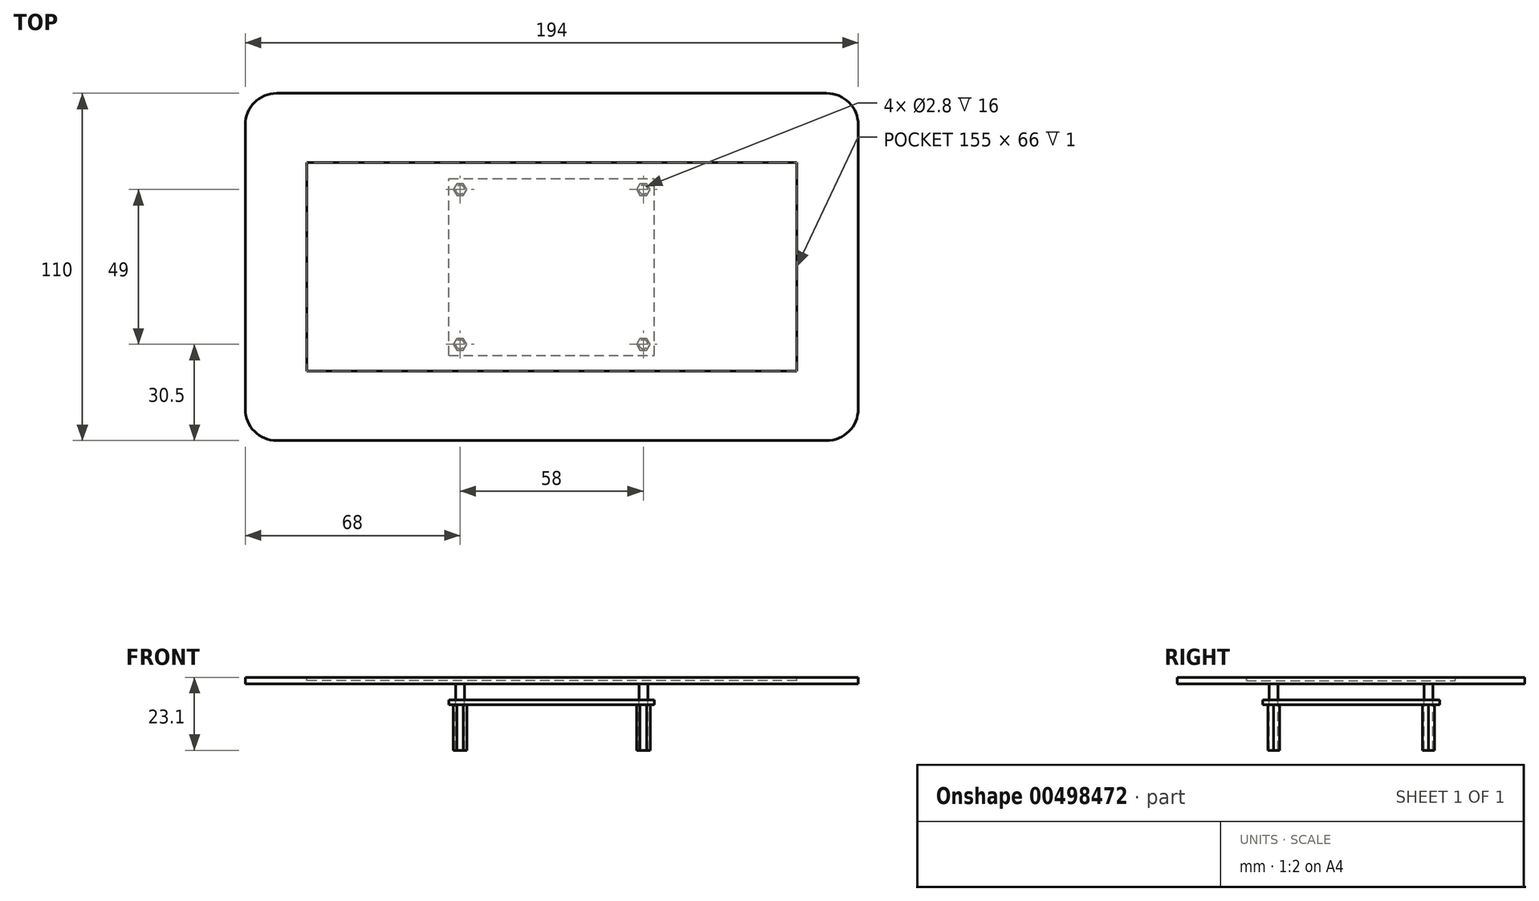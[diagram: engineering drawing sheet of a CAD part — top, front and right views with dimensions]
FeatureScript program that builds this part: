
annotation { "Feature Type Name" : "Feature", "Feature Type Description" : "" }
export const myFeature = defineFeature(function(context is Context, id is Id, definition is map)
    precondition{}
    {
        {
            var Q0;
            Q0=qCreatedBy(makeId("Top.planeOp"),FACE);
            var sketch = newSketch(context, id + "F0", { "sketchPlane" : qUnion([Q0])});
            skLineSegment(sketch, "E0.bottom", {"start": v(-87, 55) * mm, "end": v(87, 55) * mm});
            skLineSegment(sketch, "E0.top", {"start": v(-87, -55) * mm, "end": v(87, -55) * mm});
            skLineSegment(sketch, "E0.left", {"start": v(-97, 45) * mm, "end": v(-97, -45) * mm});
            skLineSegment(sketch, "E0.right", {"start": v(97, 45) * mm, "end": v(97, -45) * mm});
            skPoint(sketch, "E0.middle", {"position": v(0, 0) * mm});
            skPoint(sketch, "E1.visualSharp", {"position": v(-97, 55) * mm});
            skArc(sketch, "E1.filletArc", {"start": v(-87, 55) * mm, "mid": v(-94.07, 52.07) * mm, "end": v(-97, 45) * mm});
            skPoint(sketch, "E2.visualSharp", {"position": v(-97, -55) * mm});
            skArc(sketch, "E2.filletArc", {"start": v(-97, -45) * mm, "mid": v(-94.07, -52.07) * mm, "end": v(-87, -55) * mm});
            skPoint(sketch, "E3.visualSharp", {"position": v(97, -55) * mm});
            skArc(sketch, "E3.filletArc", {"start": v(87, -55) * mm, "mid": v(94.07, -52.07) * mm, "end": v(97, -45) * mm});
            skPoint(sketch, "E4.visualSharp", {"position": v(97, 55) * mm});
            skArc(sketch, "E4.filletArc", {"start": v(97, 45) * mm, "mid": v(94.07, 52.07) * mm, "end": v(87, 55) * mm});
            skSolve(sketch);
        }
        {
            var Q0;
            Q0 = qSketchRegion(id + "F0", true);
            extrude(context, id + "F1", {"entities" : qUnion([Q0]), "depth" : 2 * mm});
        }
        {
            var Q0;
            Q0=makeQuery(id+"F1.opExtrude","CAP_FACE",FACE,{"disambiguationData":[OSD([sQuery(id+"F0.wireOp",EDGE,"E0.bottom"),sQuery(id+"F0.wireOp",EDGE,"E0.top"),sQuery(id+"F0.wireOp",EDGE,"E0.left"),sQuery(id+"F0.wireOp",EDGE,"E0.right"),sQuery(id+"F0.wireOp",EDGE,"E1.filletArc"),sQuery(id+"F0.wireOp",EDGE,"E2.filletArc"),sQuery(id+"F0.wireOp",EDGE,"E3.filletArc"),sQuery(id+"F0.wireOp",EDGE,"E4.filletArc")])],"isStart":false});
            var sketch = newSketch(context, id + "F2", { "sketchPlane" : qUnion([Q0])});
            skLineSegment(sketch, "E5.bottom", {"start": v(77.5, -33) * mm, "end": v(-77.5, -33) * mm});
            skLineSegment(sketch, "E5.top", {"start": v(77.5, 33) * mm, "end": v(-77.5, 33) * mm});
            skLineSegment(sketch, "E5.left", {"start": v(77.5, -33) * mm, "end": v(77.5, 33) * mm});
            skLineSegment(sketch, "E5.right", {"start": v(-77.5, -33) * mm, "end": v(-77.5, 33) * mm});
            skPoint(sketch, "E5.middle", {"position": v(0, 0) * mm});
            skSolve(sketch);
        }
        {
            var Q0;
            Q0=makeQuery(id+"F2.imprint","IMPRINT",FACE,{"disambiguationData":[TD([[makeQuery(id+"F2.imprint","IMPRINT",EDGE,{"derivedFrom":sQuery(id+"F2.wireOp",EDGE,"E5.bottom")}),-1.0]])]});
            extrude(context, id + "F3", {"entities" : qUnion([Q0]), "operationType" : NewBodyOperationType.REMOVE, "oppositeDirection" : true, "depth" : 1 * mm});
        }
        {
            var Q0;
            Q0=makeQuery(id+"F1.opExtrude","CAP_FACE",FACE,{"disambiguationData":[OSD([sQuery(id+"F0.wireOp",EDGE,"E0.bottom"),sQuery(id+"F0.wireOp",EDGE,"E0.top"),sQuery(id+"F0.wireOp",EDGE,"E0.left"),sQuery(id+"F0.wireOp",EDGE,"E0.right"),sQuery(id+"F0.wireOp",EDGE,"E1.filletArc"),sQuery(id+"F0.wireOp",EDGE,"E2.filletArc"),sQuery(id+"F0.wireOp",EDGE,"E3.filletArc"),sQuery(id+"F0.wireOp",EDGE,"E4.filletArc")])],"isStart":true});
            var sketch = newSketch(context, id + "F4", { "sketchPlane" : qUnion([Q0])});
            skLineSegment(sketch, "E6.bottom", {"start": v(-29, 24.5) * mm, "end": v(29, 24.5) * mm, "construction": true});
            skLineSegment(sketch, "E6.top", {"start": v(-29, -24.5) * mm, "end": v(29, -24.5) * mm, "construction": true});
            skLineSegment(sketch, "E6.left", {"start": v(-29, 24.5) * mm, "end": v(-29, -24.5) * mm, "construction": true});
            skLineSegment(sketch, "E6.right", {"start": v(29, 24.5) * mm, "end": v(29, -24.5) * mm, "construction": true});
            skPoint(sketch, "E6.middle", {"position": v(0, 0) * mm});
            skCircle(sketch, "E7", {"center": v(-29, 24.5) * mm, "radius": 1.4 * mm});
            skCircle(sketch, "E8", {"center": v(29, 24.5) * mm, "radius": 1.4 * mm});
            skCircle(sketch, "E9", {"center": v(-29, -24.5) * mm, "radius": 1.4 * mm});
            skCircle(sketch, "E10", {"center": v(29, -24.5) * mm, "radius": 1.4 * mm});
            skSolve(sketch);
        }
        {
            var Q0;
            Q0=makeQuery(id+"F4.imprint","IMPRINT",FACE,{"disambiguationData":[TD([[makeQuery(id+"F4.imprint","IMPRINT",EDGE,{"derivedFrom":sQuery(id+"F4.wireOp",EDGE,"E7")}),1.0]])]});
            var Q1;
            Q1=makeQuery(id+"F4.imprint","IMPRINT",FACE,{"disambiguationData":[TD([[makeQuery(id+"F4.imprint","IMPRINT",EDGE,{"derivedFrom":sQuery(id+"F4.wireOp",EDGE,"E9")}),1.0]])]});
            var Q2;
            Q2=makeQuery(id+"F4.imprint","IMPRINT",FACE,{"disambiguationData":[TD([[makeQuery(id+"F4.imprint","IMPRINT",EDGE,{"derivedFrom":sQuery(id+"F4.wireOp",EDGE,"E10")}),1.0]])]});
            var Q3;
            Q3=makeQuery(id+"F4.imprint","IMPRINT",FACE,{"disambiguationData":[TD([[makeQuery(id+"F4.imprint","IMPRINT",EDGE,{"derivedFrom":sQuery(id+"F4.wireOp",EDGE,"E8")}),1.0]])]});
            extrude(context, id + "F5", {"entities" : qUnion([Q0, Q1, Q2, Q3]), "operationType" : NewBodyOperationType.ADD, "depth" : 5.1 * mm});
        }
        {
            var Q0;
            Q0=makeQuery(id+"F5.opExtrude","CAP_FACE",FACE,{"disambiguationData":[OSD([sQuery(id+"F4.wireOp",EDGE,"E7")])],"isStart":false});
            var sketch = newSketch(context, id + "F6", { "sketchPlane" : qUnion([Q0])});
            skLineSegment(sketch, "E11.bottom", {"start": v(-29, 24.5) * mm, "end": v(29, 24.5) * mm, "construction": true});
            skLineSegment(sketch, "E11.top", {"start": v(-29, -24.5) * mm, "end": v(29, -24.5) * mm, "construction": true});
            skLineSegment(sketch, "E11.left", {"start": v(-29, 24.5) * mm, "end": v(-29, -24.5) * mm, "construction": true});
            skLineSegment(sketch, "E11.right", {"start": v(29, 24.5) * mm, "end": v(29, -24.5) * mm, "construction": true});
            skPoint(sketch, "E11.middle", {"position": v(0, 0) * mm});
            skLineSegment(sketch, "E12.bottom", {"start": v(-32.5, 28) * mm, "end": v(32.5, 28) * mm});
            skLineSegment(sketch, "E12.top", {"start": v(-32.5, -28) * mm, "end": v(32.5, -28) * mm});
            skLineSegment(sketch, "E12.left", {"start": v(-32.5, 28) * mm, "end": v(-32.5, -28) * mm});
            skLineSegment(sketch, "E12.right", {"start": v(32.5, 28) * mm, "end": v(32.5, -28) * mm});
            skCircle(sketch, "E13", {"center": v(-29, 24.5) * mm, "radius": 1.4 * mm});
            skCircle(sketch, "E14", {"center": v(29, 24.5) * mm, "radius": 1.4 * mm});
            skCircle(sketch, "E15", {"center": v(-29, -24.5) * mm, "radius": 1.4 * mm});
            skCircle(sketch, "E16", {"center": v(29, -24.5) * mm, "radius": 1.4 * mm});
            skSolve(sketch);
        }
        {
            var Q0;
            Q0 = qSketchRegion(id + "F6", true);
            extrude(context, id + "F7", {"entities" : qUnion([Q0]), "depth" : 1.6 * mm});
        }
        {
            var Q0;
            Q0=makeQuery(id+"F7.opExtrude","CAP_FACE",FACE,{"disambiguationData":[OSD([sQuery(id+"F6.wireOp",EDGE,"E12.bottom"),sQuery(id+"F6.wireOp",EDGE,"E12.top"),sQuery(id+"F6.wireOp",EDGE,"E12.left"),sQuery(id+"F6.wireOp",EDGE,"E12.right"),sQuery(id+"F6.wireOp",EDGE,"E13"),sQuery(id+"F6.wireOp",EDGE,"E14"),sQuery(id+"F6.wireOp",EDGE,"E15"),sQuery(id+"F6.wireOp",EDGE,"E16")])],"isStart":false});
            var sketch = newSketch(context, id + "F8", { "sketchPlane" : qUnion([Q0])});
            skCircle(sketch, "E17", {"center": v(-29, 24.5) * mm, "radius": 1.4 * mm});
            skCircle(sketch, "E18", {"center": v(29, 24.5) * mm, "radius": 1.4 * mm});
            skCircle(sketch, "E19", {"center": v(-29, -24.5) * mm, "radius": 1.4 * mm});
            skCircle(sketch, "E20", {"center": v(29, -24.5) * mm, "radius": 1.4 * mm});
            skCircle(sketch, "E21.cCircle", {"center": v(-29, 24.5) * mm, "radius": 2.15 * mm, "construction": true});
            skLineSegment(sketch, "E21.0", {"start": v(-26.85, 24.5) * mm, "end": v(-27.92, 22.64) * mm});
            skLineSegment(sketch, "E21.1", {"start": v(-27.92, 22.64) * mm, "end": v(-30.07, 22.64) * mm});
            skLineSegment(sketch, "E21.2", {"start": v(-30.07, 22.64) * mm, "end": v(-31.15, 24.5) * mm});
            skLineSegment(sketch, "E21.3", {"start": v(-31.15, 24.5) * mm, "end": v(-30.07, 26.36) * mm});
            skLineSegment(sketch, "E21.4", {"start": v(-30.07, 26.36) * mm, "end": v(-27.92, 26.36) * mm});
            skLineSegment(sketch, "E21.5", {"start": v(-27.92, 26.36) * mm, "end": v(-26.85, 24.5) * mm});
            skCircle(sketch, "E22.cCircle", {"center": v(29, 24.5) * mm, "radius": 2.15 * mm, "construction": true});
            skLineSegment(sketch, "E22.0", {"start": v(26.85, 24.5) * mm, "end": v(27.93, 26.36) * mm});
            skLineSegment(sketch, "E22.1", {"start": v(27.93, 26.36) * mm, "end": v(30.07, 26.36) * mm});
            skLineSegment(sketch, "E22.2", {"start": v(30.07, 26.36) * mm, "end": v(31.15, 24.5) * mm});
            skLineSegment(sketch, "E22.3", {"start": v(31.15, 24.5) * mm, "end": v(30.08, 22.64) * mm});
            skLineSegment(sketch, "E22.4", {"start": v(30.07, 22.64) * mm, "end": v(27.92, 22.64) * mm});
            skLineSegment(sketch, "E22.5", {"start": v(27.93, 22.64) * mm, "end": v(26.85, 24.5) * mm});
            skCircle(sketch, "E23.cCircle", {"center": v(29, -24.5) * mm, "radius": 2.15 * mm, "construction": true});
            skLineSegment(sketch, "E23.0", {"start": v(26.85, -24.5) * mm, "end": v(27.92, -22.64) * mm});
            skLineSegment(sketch, "E23.1", {"start": v(27.93, -22.64) * mm, "end": v(30.08, -22.64) * mm});
            skLineSegment(sketch, "E23.2", {"start": v(30.07, -22.64) * mm, "end": v(31.15, -24.5) * mm});
            skLineSegment(sketch, "E23.3", {"start": v(31.15, -24.5) * mm, "end": v(30.07, -26.36) * mm});
            skLineSegment(sketch, "E23.4", {"start": v(30.08, -26.36) * mm, "end": v(27.92, -26.36) * mm});
            skLineSegment(sketch, "E23.5", {"start": v(27.93, -26.36) * mm, "end": v(26.85, -24.5) * mm});
            skCircle(sketch, "E24.cCircle", {"center": v(-29, -24.5) * mm, "radius": 2.15 * mm, "construction": true});
            skLineSegment(sketch, "E24.0", {"start": v(-26.85, -24.5) * mm, "end": v(-27.93, -26.36) * mm});
            skLineSegment(sketch, "E24.1", {"start": v(-27.93, -26.36) * mm, "end": v(-30.07, -26.36) * mm});
            skLineSegment(sketch, "E24.2", {"start": v(-30.08, -26.36) * mm, "end": v(-31.15, -24.5) * mm});
            skLineSegment(sketch, "E24.3", {"start": v(-31.15, -24.5) * mm, "end": v(-30.08, -22.64) * mm});
            skLineSegment(sketch, "E24.4", {"start": v(-30.08, -22.64) * mm, "end": v(-27.92, -22.64) * mm});
            skLineSegment(sketch, "E24.5", {"start": v(-27.93, -22.64) * mm, "end": v(-26.85, -24.5) * mm});
            skSolve(sketch);
        }
        {
            var Q0;
            Q0 = qSketchRegion(id + "F8", true);
            extrude(context, id + "F9", {"entities" : qUnion([Q0]), "operationType" : NewBodyOperationType.ADD, "depth" : 14.4 * mm});
        }
    });
